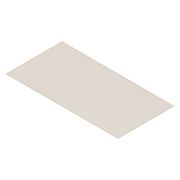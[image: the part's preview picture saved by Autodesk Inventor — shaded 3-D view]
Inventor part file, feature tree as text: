
AUTODESK INVENTOR PART (.ipt)
format: ipt  version: 2012 (Build 160160000, 160)  size: 67,584 bytes
history: native  units: in
note: dims shown in document units (in); Inventor stores cm internally (conversion verified against a paired STEP export)
features: extrude x1, sketch x1
ambient origin geometry x8: Origin, YZ Plane, XZ Plane, XY Plane, X Axis, Y Axis, Z Axis, Center Point
bodies: Solid1 (feature_tree)
feature tree (2):
  extrude  "Extrusion1"  Depth=12.0in
  sketch  "Sketch2"  dims[d0=24.0in d1=12.0in d4=0.0625in d5=0.0in]
